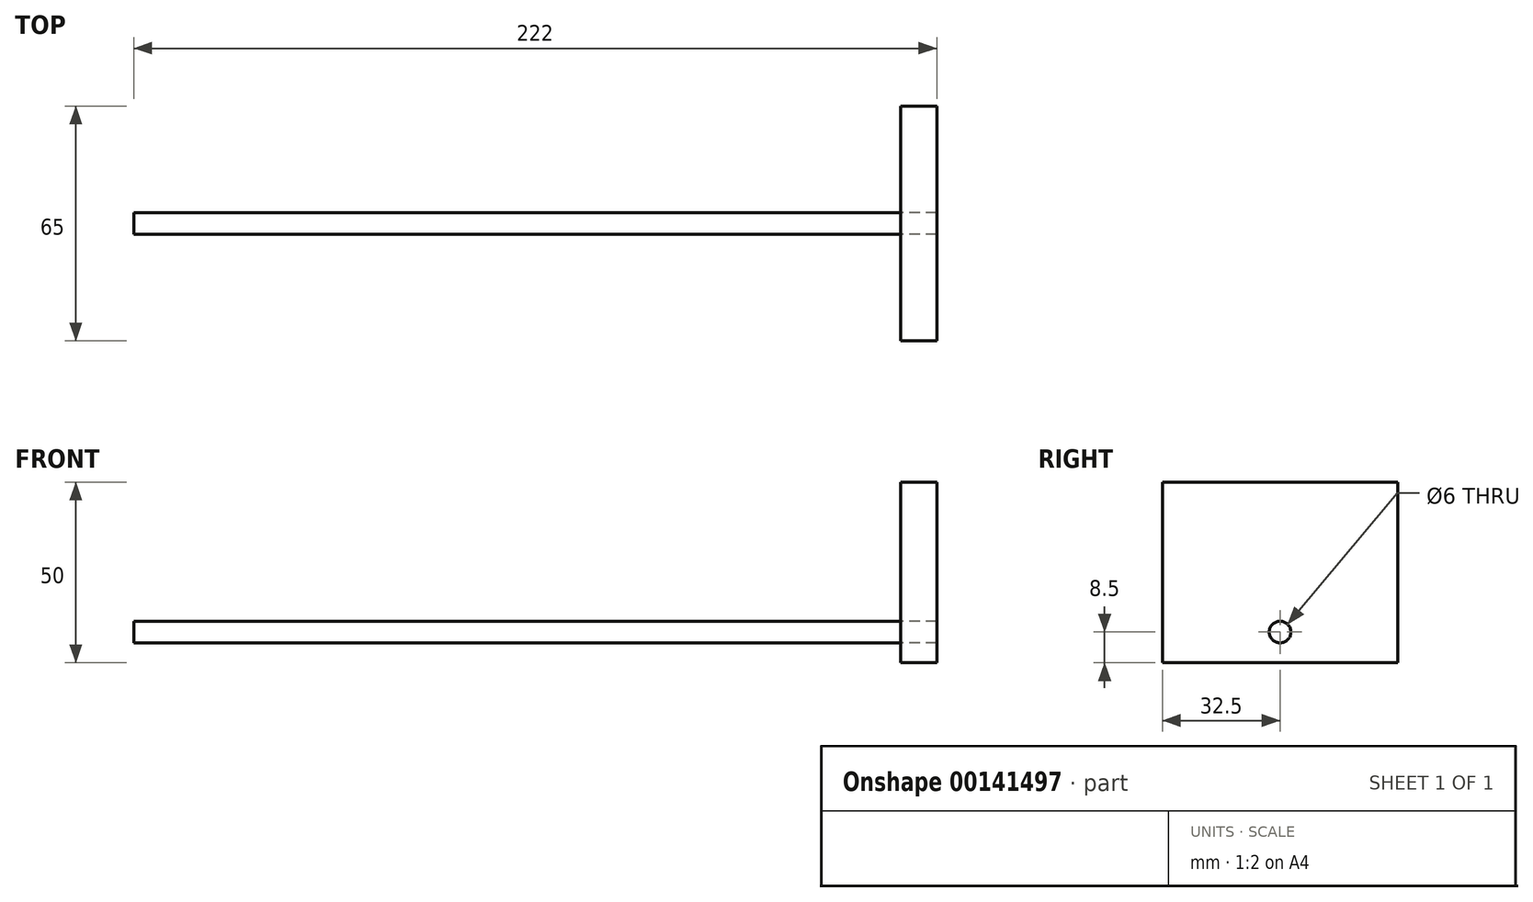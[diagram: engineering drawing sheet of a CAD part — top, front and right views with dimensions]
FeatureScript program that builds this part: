
annotation { "Feature Type Name" : "Feature", "Feature Type Description" : "" }
export const myFeature = defineFeature(function(context is Context, id is Id, definition is map)
    precondition{}
    {
        {
            var Q0;
            Q0=qCreatedBy(makeId("Right.planeOp"),FACE);
            var sketch = newSketch(context, id + "F0", { "sketchPlane" : qUnion([Q0])});
            skCircle(sketch, "E0", {"center": v(0, -20) * mm, "radius": 3 * mm});
            skSolve(sketch);
        }
        {
            var Q0;
            Q0 = qSketchRegion(id + "F0", true);
            extrude(context, id + "F1", {"entities" : qUnion([Q0]), "depth" : 212 * mm});
        }
        {
            var Q0;
            Q0=makeQuery(id+"F1.opExtrude","CAP_FACE",FACE,{"disambiguationData":[OSD([sQuery(id+"F0.wireOp",EDGE,"E0")])],"isStart":false});
            var sketch = newSketch(context, id + "F2", { "sketchPlane" : qUnion([Q0])});
            skLineSegment(sketch, "E1.bottom", {"start": v(-32.5, 21.5) * mm, "end": v(32.5, 21.5) * mm});
            skLineSegment(sketch, "E1.top", {"start": v(-32.5, -28.5) * mm, "end": v(32.5, -28.5) * mm});
            skLineSegment(sketch, "E1.left", {"start": v(-32.5, 21.5) * mm, "end": v(-32.5, -28.5) * mm});
            skLineSegment(sketch, "E1.right", {"start": v(32.5, 21.5) * mm, "end": v(32.5, -28.5) * mm});
            skSolve(sketch);
        }
        {
            var Q0;
            Q0=makeQuery(id+"F2.imprint","IMPRINT",FACE,{"disambiguationData":[TD([[makeQuery(id+"F2.imprint","IMPRINT",EDGE,{"derivedFrom":sQuery(id+"F2.wireOp",EDGE,"E1.bottom")}),-1.0]])]});
            extrude(context, id + "F3", {"entities" : qUnion([Q0]), "operationType" : NewBodyOperationType.ADD, "depth" : 10 * mm});
        }
    });
